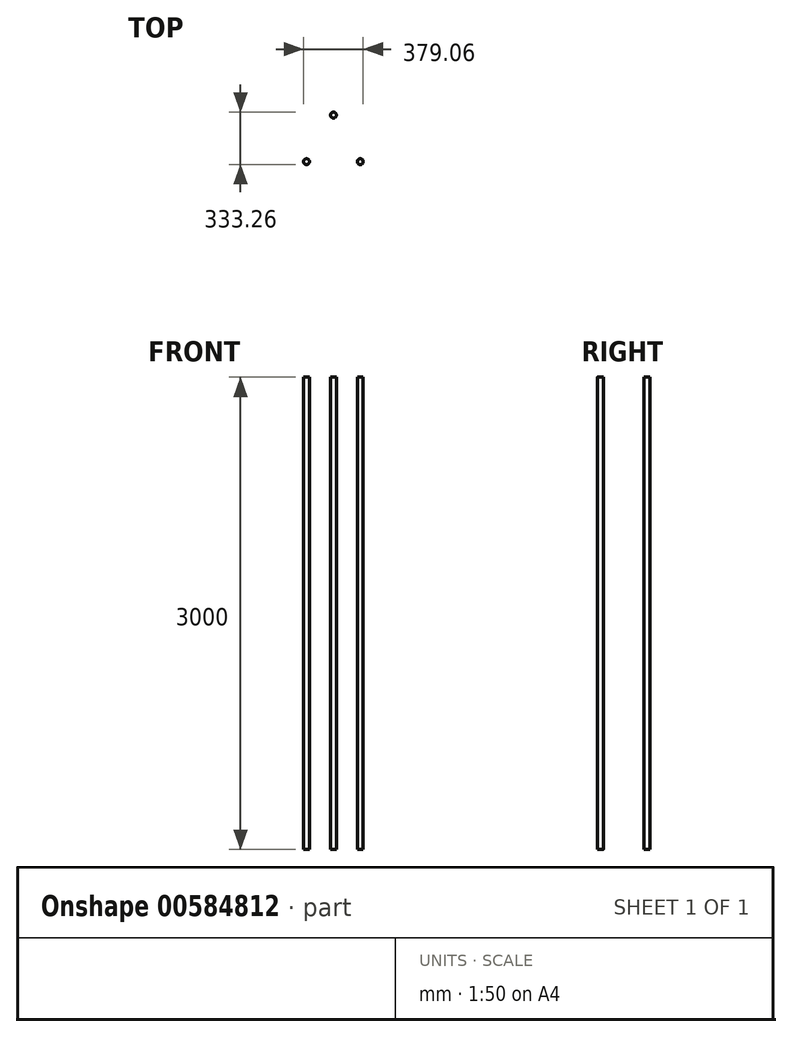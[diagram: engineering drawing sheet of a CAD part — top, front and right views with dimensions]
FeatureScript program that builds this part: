
annotation { "Feature Type Name" : "Feature", "Feature Type Description" : "" }
export const myFeature = defineFeature(function(context is Context, id is Id, definition is map)
    precondition{}
    {
        {
            var Q0;
            Q0=qCreatedBy(makeId("Top.planeOp"),FACE);
            var sketch = newSketch(context, id + "F0", { "sketchPlane" : qUnion([Q0])});
            skCircle(sketch, "E0", {"center": v(0, 197.36) * mm, "radius": 18.61 * mm});
            skCircle(sketch, "E1.1.0", {"center": v(-170.92, -98.68) * mm, "radius": 18.61 * mm});
            skCircle(sketch, "E1.2.0", {"center": v(170.92, -98.68) * mm, "radius": 18.61 * mm});
            skPoint(sketch, "E1.center", {"position": v(0, 0) * mm});
            skSolve(sketch);
        }
        {
            var Q0;
            Q0=sQuery(id+"F0.wireOp",EDGE,"E0");
            var Q1;
            Q1=sQuery(id+"F0.wireOp",EDGE,"E1.1.0");
            var Q2;
            Q2=sQuery(id+"F0.wireOp",EDGE,"E1.2.0");
            extrude(context, id + "F1", {"bodyType" : ToolBodyType.SURFACE, "surfaceEntities" : qUnion([Q0, Q1, Q2]), "depth" : 3000 * mm, "offsetDistance" : 25 * mm});
        }
    });
